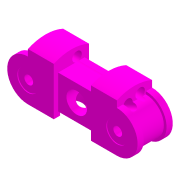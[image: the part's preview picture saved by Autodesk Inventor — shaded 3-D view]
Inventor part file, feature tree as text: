
AUTODESK INVENTOR PART (.ipt)
format: ipt  version: 2020 (Build 240168000, 168)  size: 292,864 bytes
history: native  units: mm
features: extrude x11, sketch x11, plane x3, mirror x2, projected_geometry x2, direct_edit x1, other x1
ambient origin geometry x8: Origin, YZ Plane, XZ Plane, XY Plane, X Axis, Y Axis, Z Axis, Center Point
bodies: Solid1 (feature_tree)
feature tree (31):
  extrude  "Extrusion1"  Depth=8.15mm
  extrude  "Extrusion2"  Depth=3.25mm
  mirror  "Mirror1"
  extrude  "Extrusion3"  Depth=9.25mm
  extrude  "Extrusion4"  Depth=6.25mm TaperAngle=0.0deg
  extrude  "Extrusion5"  Depth=10.0mm TaperAngle=0.0deg
  plane  "Work Plane1"
  extrude  "Extrusion6"  Depth=2.12mm
  extrude  "Extrusion7"  Depth=8.7mm
  plane  "Work Plane2"
  extrude  "Extrusion8"  Depth=5.0mm
  plane  "Work Plane3"
  extrude  "Extrusion9"  Depth=0.65mm
  extrude  "Extrusion10"  Depth=3.0mm
  extrude  "Extrusion11"  Depth=10.0mm
  mirror  "Mirror2"
  direct_edit  "Direct Edit1"
  sketch  "Sketch1"  dims[d0=9.0mm d1=8.15mm]
  sketch  "Sketch2"  dims[d2=6.4mm d3=0.0mm d4=3.25mm]
  sketch  "Sketch3"  dims[d5=4.25mm d6=9.25mm]
  sketch  "Sketch4"  dims[d8=0.0mm d9=6.25mm d10=0.0mm]
  sketch  "Sketch5"  dims[d11=10.0mm d12=6.25mm d13=0.0mm]
  sketch  "Sketch6"  dims[d14=13.879mm d15=0.0mm d16=2.12mm]
  sketch  "Sketch7"  dims[d17=0.0mm d18=0.0mm d19=8.7mm]
  sketch  "Sketch8"  dims[d20=5.5mm d21=0.0mm d22=5.0mm]
  projected_geometry  "Projected Loop1"
  sketch  "Sketch9"  dims[d23=0.0mm d24=0.0mm d25=0.65mm]
  projected_geometry  "Projected Loop2"
  sketch  "Sketch10"  dims[d26=6.981317mm d27=3.0mm]
  sketch  "Sketch11"  dims[d28=5.5mm d29=0.0mm d30=4.363323mm d31=2.3mm d32=5.5mm d33=11.25mm d34=0.0mm d35=0.0mm d36=2.3mm d37=1.219mm d38=0.0mm d39=5.15mm d40=0.2mm d41=0.0mm d42=8.0mm d43=10.0mm d44=10.0mm]
  other  "Scale1"
